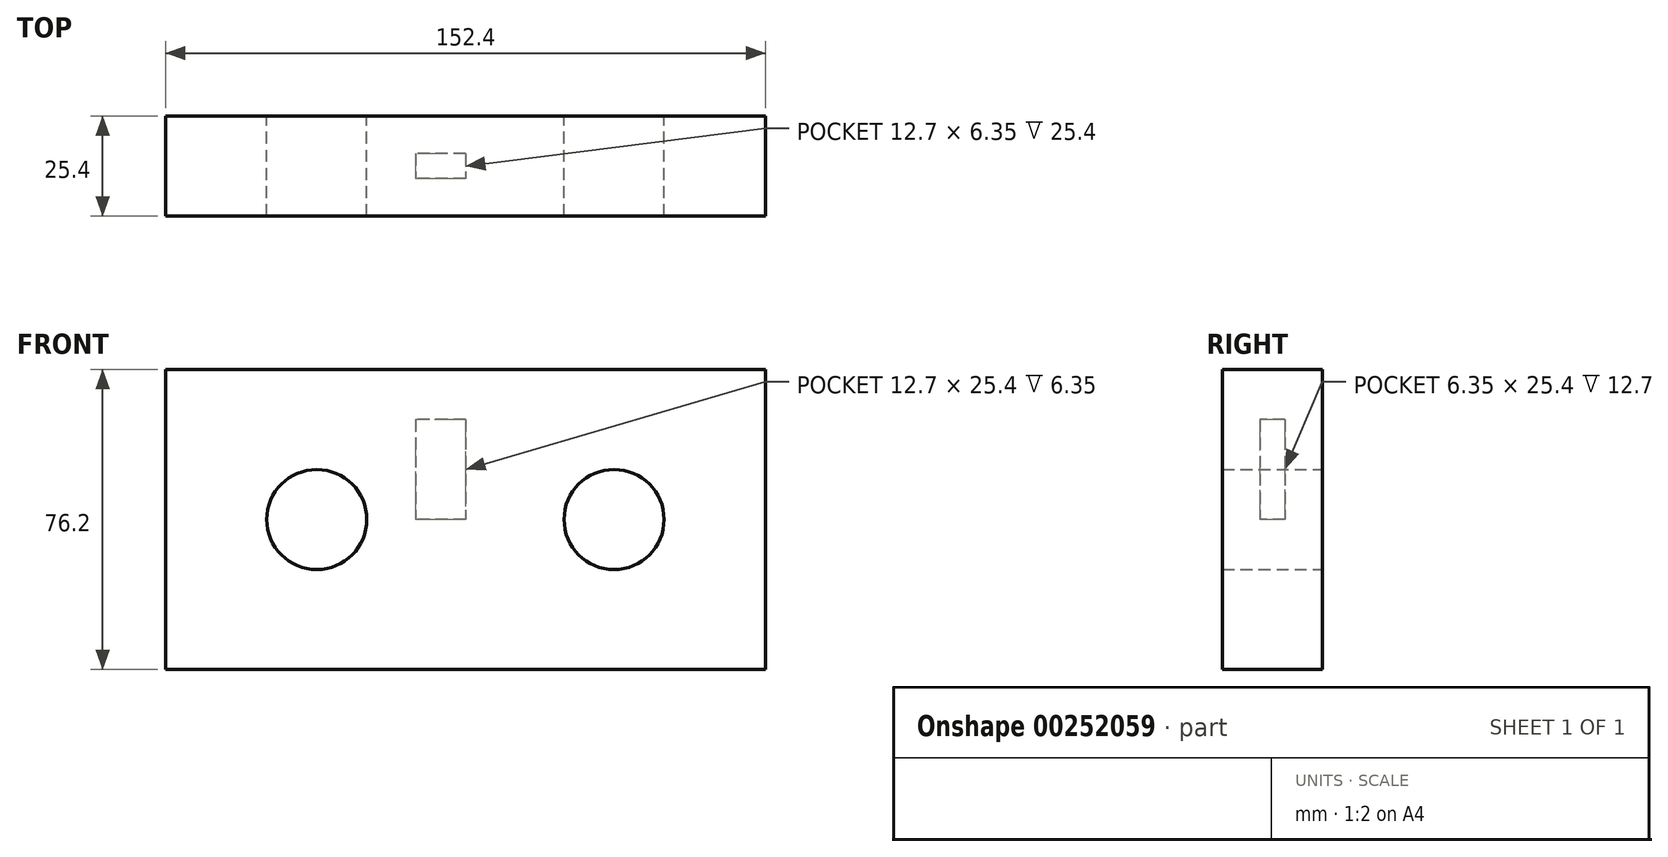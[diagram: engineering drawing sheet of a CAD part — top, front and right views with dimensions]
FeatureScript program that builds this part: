
annotation { "Feature Type Name" : "Feature", "Feature Type Description" : "" }
export const myFeature = defineFeature(function(context is Context, id is Id, definition is map)
    precondition{}
    {
        {
            var Q0;
            Q0=qCreatedBy(makeId("Front.planeOp"),FACE);
            var sketch = newSketch(context, id + "F0", { "sketchPlane" : qUnion([Q0])});
            skLineSegment(sketch, "E0.bottom", {"start": v(76.2, 38.1) * mm, "end": v(-76.2, 38.1) * mm});
            skLineSegment(sketch, "E0.top", {"start": v(76.2, -38.1) * mm, "end": v(-76.2, -38.1) * mm});
            skLineSegment(sketch, "E0.left", {"start": v(76.2, 38.1) * mm, "end": v(76.2, -38.1) * mm});
            skLineSegment(sketch, "E0.right", {"start": v(-76.2, 38.1) * mm, "end": v(-76.2, -38.1) * mm});
            skPoint(sketch, "E0.middle", {"position": v(0, 0) * mm});
            skSolve(sketch);
        }
        {
            var Q0;
            Q0=makeQuery(id+"F0.imprint","IMPRINT",FACE,{"disambiguationData":[TD([[makeQuery(id+"F0.imprint","IMPRINT",EDGE,{"derivedFrom":sQuery(id+"F0.wireOp",EDGE,"E0.bottom")}),1.0]])]});
            var sketch = newSketch(context, id + "F1", { "sketchPlane" : qUnion([Q0])});
            skCircle(sketch, "E1", {"center": v(-37.8, 0) * mm, "radius": 12.7 * mm});
            skSolve(sketch);
        }
        {
            var Q0;
            Q0=makeQuery(id+"F0.imprint","IMPRINT",FACE,{"disambiguationData":[TD([[makeQuery(id+"F0.imprint","IMPRINT",EDGE,{"derivedFrom":sQuery(id+"F0.wireOp",EDGE,"E0.bottom")}),1.0]])]});
            var sketch = newSketch(context, id + "F2", { "sketchPlane" : qUnion([Q0])});
            skCircle(sketch, "E2", {"center": v(37.72, 0) * mm, "radius": 12.7 * mm});
            skSolve(sketch);
        }
        {
            var Q0;
            Q0=qCreatedBy(makeId("Top.planeOp"),FACE);
            var sketch = newSketch(context, id + "F3", { "sketchPlane" : qUnion([Q0])});
            skLineSegment(sketch, "E3", {"start": v(0, 0) * mm, "end": v(0, -9.53) * mm});
            skLineSegment(sketch, "E4.bottom", {"start": v(0, -9.53) * mm, "end": v(-12.7, -9.53) * mm});
            skLineSegment(sketch, "E4.top", {"start": v(0, -15.88) * mm, "end": v(-12.7, -15.88) * mm});
            skLineSegment(sketch, "E4.left", {"start": v(0, -9.53) * mm, "end": v(0, -15.88) * mm});
            skLineSegment(sketch, "E4.right", {"start": v(-12.7, -9.53) * mm, "end": v(-12.7, -15.88) * mm});
            skSolve(sketch);
        }
        {
            var Q0;
            Q0 = qSketchRegion(id + "F0", true);
            var Q1;
            Q1 = qSketchRegion(id + "F1", true);
            var Q2;
            Q2 = qSketchRegion(id + "F2", true);
            extrude(context, id + "F4", {"entities" : qUnion([Q0, Q1, Q2]), "depth" : 25.4 * mm});
        }
        {
            var Q0;
            Q0 = qSketchRegion(id + "F3", true);
            extrude(context, id + "F5", {"entities" : qUnion([Q0]), "operationType" : NewBodyOperationType.REMOVE, "depth" : 25.4 * mm});
        }
    });
